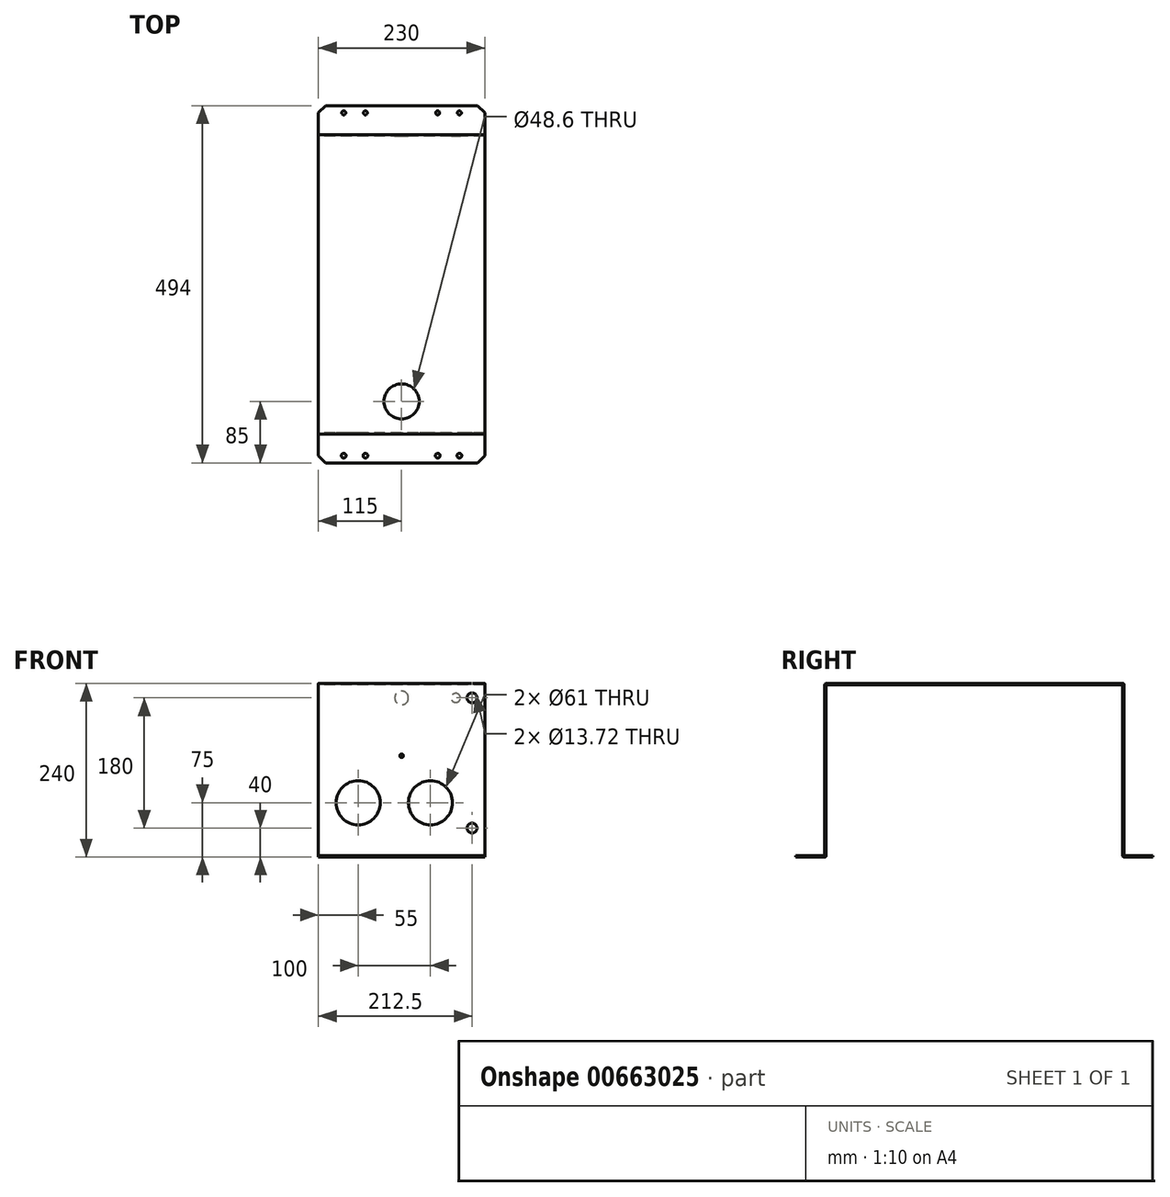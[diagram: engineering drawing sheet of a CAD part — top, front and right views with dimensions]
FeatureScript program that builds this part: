
annotation { "Feature Type Name" : "Feature", "Feature Type Description" : "" }
export const myFeature = defineFeature(function(context is Context, id is Id, definition is map)
    precondition{}
    {
        {
            var Q0;
            Q0=qCreatedBy(makeId("Right.planeOp"),FACE);
            var sketch = newSketch(context, id + "F0", { "sketchPlane" : qUnion([Q0])});
            skLineSegment(sketch, "E0", {"start": v(-205, 0) * mm, "end": v(205, 0) * mm});
            skLineSegment(sketch, "E1", {"start": v(207, -2) * mm, "end": v(207, -238) * mm});
            skLineSegment(sketch, "E2", {"start": v(-207, -2) * mm, "end": v(-207, -238) * mm});
            skLineSegment(sketch, "E3", {"start": v(-207, -238) * mm, "end": v(-247, -238) * mm});
            skLineSegment(sketch, "E4", {"start": v(207, -238) * mm, "end": v(247, -238) * mm});
            skLineSegment(sketch, "E5.0", {"start": v(207, -240) * mm, "end": v(247, -240) * mm});
            skLineSegment(sketch, "E5.1", {"start": v(-207, -240) * mm, "end": v(-247, -240) * mm});
            skLineSegment(sketch, "E5.2", {"start": v(-205, -2) * mm, "end": v(-205, -238) * mm});
            skLineSegment(sketch, "E5.3", {"start": v(-205, -2) * mm, "end": v(205, -2) * mm});
            skLineSegment(sketch, "E5.4", {"start": v(205, -2) * mm, "end": v(205, -238) * mm});
            skLineSegment(sketch, "E6", {"start": v(247, -238) * mm, "end": v(247, -240) * mm});
            skLineSegment(sketch, "E7", {"start": v(-247, -238) * mm, "end": v(-247, -240) * mm});
            skPoint(sketch, "E8.visualSharp", {"position": v(-207, 0) * mm});
            skArc(sketch, "E8.filletArc", {"start": v(-205, 0) * mm, "mid": v(-206.41, -0.59) * mm, "end": v(-207, -2) * mm});
            skPoint(sketch, "E9.visualSharp", {"position": v(207, 0) * mm});
            skArc(sketch, "E9.filletArc", {"start": v(207, -2) * mm, "mid": v(206.41, -0.59) * mm, "end": v(205, 0) * mm});
            skPoint(sketch, "E10.visualSharp", {"position": v(205, -240) * mm});
            skArc(sketch, "E10.filletArc", {"start": v(205, -238) * mm, "mid": v(205.59, -239.41) * mm, "end": v(207, -240) * mm});
            skPoint(sketch, "E11.visualSharp", {"position": v(-205, -240) * mm});
            skArc(sketch, "E11.filletArc", {"start": v(-207, -240) * mm, "mid": v(-205.59, -239.41) * mm, "end": v(-205, -238) * mm});
            skSolve(sketch);
        }
        {
            var Q0;
            Q0=makeQuery(id+"F0.imprint","IMPRINT",FACE,{"disambiguationData":[TD([[makeQuery(id+"F0.imprint","IMPRINT",EDGE,{"derivedFrom":sQuery(id+"F0.wireOp",EDGE,"E0")}),-1.0]])]});
            extrude(context, id + "F1", {"entities" : qUnion([Q0]), "depth" : 230 * mm, "offsetDistance" : 25 * mm});
        }
        {
            var Q0;
            Q0=makeQuery(id+"F1.opExtrude","SWEPT_FACE",FACE,{"disambiguationData":[OSD([sQuery(id+"F0.wireOp",EDGE,"E0")])]});
            var sketch = newSketch(context, id + "F2", { "sketchPlane" : qUnion([Q0])});
            skPoint(sketch, "E12", {"position": v(115, -162) * mm});
            skSolve(sketch);
        }
        {
            var Q0;
            Q0=sQuery(id+"F2.wireOp",VERTEX,"E12");
            var Q1;
            Q1=makeQuery(id+"F1.opExtrude","SWEPT_BODY",BODY,{"disambiguationData":[OSD([sQuery(id+"F0.wireOp",EDGE,"E0"),sQuery(id+"F0.wireOp",EDGE,"E1"),sQuery(id+"F0.wireOp",EDGE,"E2"),sQuery(id+"F0.wireOp",EDGE,"E3"),sQuery(id+"F0.wireOp",EDGE,"E4"),sQuery(id+"F0.wireOp",EDGE,"E5.0"),sQuery(id+"F0.wireOp",EDGE,"E5.1"),sQuery(id+"F0.wireOp",EDGE,"E5.2"),sQuery(id+"F0.wireOp",EDGE,"E5.3"),sQuery(id+"F0.wireOp",EDGE,"E5.4"),sQuery(id+"F0.wireOp",EDGE,"E6"),sQuery(id+"F0.wireOp",EDGE,"E7"),sQuery(id+"F0.wireOp",EDGE,"E8.filletArc"),sQuery(id+"F0.wireOp",EDGE,"E9.filletArc"),sQuery(id+"F0.wireOp",EDGE,"E10.filletArc"),sQuery(id+"F0.wireOp",EDGE,"E11.filletArc")])]});
            hole(context, id + "F3", {"style" : HoleStyle.SIMPLE, "endStyle" : HoleEndStyle.THROUGH, "holeDiameter" : 48.6 * mm, "majorDiameter" : 5 * mm, "isTappedThrough" : true, "tappedDepth" : 12 * mm, "tapClearance" : 3, "locations" : qUnion([Q0]), "scope" : qUnion([Q1])});
        }
        {
            var Q0;
            Q0=makeQuery(id+"F1.opExtrude","SWEPT_FACE",FACE,{"disambiguationData":[OSD([sQuery(id+"F0.wireOp",EDGE,"E3")])]});
            var sketch = newSketch(context, id + "F4", { "sketchPlane" : qUnion([Q0])});
            skPoint(sketch, "E13", {"position": v(35, -237) * mm});
            skPoint(sketch, "E14", {"position": v(65, -237) * mm});
            skPoint(sketch, "E15", {"position": v(165, -237) * mm});
            skPoint(sketch, "E16", {"position": v(195, -237) * mm});
            skPoint(sketch, "E17", {"position": v(35, 237) * mm});
            skPoint(sketch, "E18", {"position": v(65, 237) * mm});
            skPoint(sketch, "E19", {"position": v(165, 237) * mm});
            skPoint(sketch, "E20", {"position": v(195, 237) * mm});
            skSolve(sketch);
        }
        {
            var Q0;
            Q0=sQuery(id+"F4.wireOp",VERTEX,"E13");
            var Q1;
            Q1=sQuery(id+"F4.wireOp",VERTEX,"E14");
            var Q2;
            Q2=sQuery(id+"F4.wireOp",VERTEX,"E15");
            var Q3;
            Q3=sQuery(id+"F4.wireOp",VERTEX,"E16");
            var Q4;
            Q4=makeQuery(id+"F1.opExtrude","SWEPT_BODY",BODY,{"disambiguationData":[OSD([sQuery(id+"F0.wireOp",EDGE,"E0"),sQuery(id+"F0.wireOp",EDGE,"E1"),sQuery(id+"F0.wireOp",EDGE,"E2"),sQuery(id+"F0.wireOp",EDGE,"E3"),sQuery(id+"F0.wireOp",EDGE,"E4"),sQuery(id+"F0.wireOp",EDGE,"E5.0"),sQuery(id+"F0.wireOp",EDGE,"E5.1"),sQuery(id+"F0.wireOp",EDGE,"E5.2"),sQuery(id+"F0.wireOp",EDGE,"E5.3"),sQuery(id+"F0.wireOp",EDGE,"E5.4"),sQuery(id+"F0.wireOp",EDGE,"E6"),sQuery(id+"F0.wireOp",EDGE,"E7"),sQuery(id+"F0.wireOp",EDGE,"E8.filletArc"),sQuery(id+"F0.wireOp",EDGE,"E9.filletArc"),sQuery(id+"F0.wireOp",EDGE,"E10.filletArc"),sQuery(id+"F0.wireOp",EDGE,"E11.filletArc")])]});
            hole(context, id + "F5", {"style" : HoleStyle.SIMPLE, "endStyle" : HoleEndStyle.THROUGH, "holeDiameter" : 6.5 * mm, "majorDiameter" : 5 * mm, "isTappedThrough" : true, "tappedDepth" : 12 * mm, "tapClearance" : 3, "locations" : qUnion([Q0, Q1, Q2, Q3]), "scope" : qUnion([Q4])});
        }
        {
            var Q0;
            Q0=sQuery(id+"F4.wireOp",VERTEX,"E17");
            var Q1;
            Q1=sQuery(id+"F4.wireOp",VERTEX,"E18");
            var Q2;
            Q2=sQuery(id+"F4.wireOp",VERTEX,"E19");
            var Q3;
            Q3=sQuery(id+"F4.wireOp",VERTEX,"E20");
            var Q4;
            Q4=makeQuery(id+"F1.opExtrude","SWEPT_BODY",BODY,{"disambiguationData":[OSD([sQuery(id+"F0.wireOp",EDGE,"E0"),sQuery(id+"F0.wireOp",EDGE,"E1"),sQuery(id+"F0.wireOp",EDGE,"E2"),sQuery(id+"F0.wireOp",EDGE,"E3"),sQuery(id+"F0.wireOp",EDGE,"E4"),sQuery(id+"F0.wireOp",EDGE,"E5.0"),sQuery(id+"F0.wireOp",EDGE,"E5.1"),sQuery(id+"F0.wireOp",EDGE,"E5.2"),sQuery(id+"F0.wireOp",EDGE,"E5.3"),sQuery(id+"F0.wireOp",EDGE,"E5.4"),sQuery(id+"F0.wireOp",EDGE,"E6"),sQuery(id+"F0.wireOp",EDGE,"E7"),sQuery(id+"F0.wireOp",EDGE,"E8.filletArc"),sQuery(id+"F0.wireOp",EDGE,"E9.filletArc"),sQuery(id+"F0.wireOp",EDGE,"E10.filletArc"),sQuery(id+"F0.wireOp",EDGE,"E11.filletArc")])]});
            hole(context, id + "F6", {"style" : HoleStyle.SIMPLE, "endStyle" : HoleEndStyle.THROUGH, "holeDiameter" : 5.5 * mm, "majorDiameter" : 5 * mm, "isTappedThrough" : true, "tappedDepth" : 12 * mm, "tapClearance" : 3, "locations" : qUnion([Q0, Q1, Q2, Q3]), "scope" : qUnion([Q4])});
        }
        {
            var Q0;
            Q0=makeQuery(id+"F1.opExtrude","CAP_EDGE",EDGE,{"disambiguationData":[OSD([sQuery(id+"F0.wireOp",EDGE,"E7")])],"isStart":true});
            var Q1;
            Q1=makeQuery(id+"F1.opExtrude","CAP_EDGE",EDGE,{"disambiguationData":[OSD([sQuery(id+"F0.wireOp",EDGE,"E7")])],"isStart":false});
            var Q2;
            Q2=makeQuery(id+"F1.opExtrude","CAP_EDGE",EDGE,{"disambiguationData":[OSD([sQuery(id+"F0.wireOp",EDGE,"E6")])],"isStart":false});
            var Q3;
            Q3=makeQuery(id+"F1.opExtrude","CAP_EDGE",EDGE,{"disambiguationData":[OSD([sQuery(id+"F0.wireOp",EDGE,"E6")])],"isStart":true});
            chamfer(context, id + "F7", {"entities" : qUnion([Q0, Q1, Q2, Q3]), "width" : 10 * mm, "tangentPropagation" : true});
        }
        {
            var Q0;
            Q0=makeQuery(id+"F1.opExtrude","SWEPT_FACE",FACE,{"disambiguationData":[OSD([sQuery(id+"F0.wireOp",EDGE,"E2")])]});
            var sketch = newSketch(context, id + "F8", { "sketchPlane" : qUnion([Q0])});
            skPoint(sketch, "E21", {"position": v(55, -165) * mm});
            skPoint(sketch, "E22", {"position": v(155, -165) * mm});
            skPoint(sketch, "E23", {"position": v(212.5, -20) * mm});
            skPoint(sketch, "E24", {"position": v(212.5, -200) * mm});
            skPoint(sketch, "E25", {"position": v(115, -100) * mm});
            skSolve(sketch);
        }
        {
            var Q0;
            Q0=sQuery(id+"F8.wireOp",VERTEX,"E21");
            var Q1;
            Q1=sQuery(id+"F8.wireOp",VERTEX,"E22");
            var Q2;
            Q2=makeQuery(id+"F1.opExtrude","SWEPT_BODY",BODY,{"disambiguationData":[OSD([sQuery(id+"F0.wireOp",EDGE,"E0"),sQuery(id+"F0.wireOp",EDGE,"E1"),sQuery(id+"F0.wireOp",EDGE,"E2"),sQuery(id+"F0.wireOp",EDGE,"E3"),sQuery(id+"F0.wireOp",EDGE,"E4"),sQuery(id+"F0.wireOp",EDGE,"E5.0"),sQuery(id+"F0.wireOp",EDGE,"E5.1"),sQuery(id+"F0.wireOp",EDGE,"E5.2"),sQuery(id+"F0.wireOp",EDGE,"E5.3"),sQuery(id+"F0.wireOp",EDGE,"E5.4"),sQuery(id+"F0.wireOp",EDGE,"E6"),sQuery(id+"F0.wireOp",EDGE,"E7"),sQuery(id+"F0.wireOp",EDGE,"E8.filletArc"),sQuery(id+"F0.wireOp",EDGE,"E9.filletArc"),sQuery(id+"F0.wireOp",EDGE,"E10.filletArc"),sQuery(id+"F0.wireOp",EDGE,"E11.filletArc")])]});
            hole(context, id + "F9", {"style" : HoleStyle.SIMPLE, "endStyle" : HoleEndStyle.BLIND, "holeDiameter" : 61 * mm, "majorDiameter" : 5 * mm, "holeDepth" : 12 * mm, "isTappedThrough" : true, "tappedDepth" : 12 * mm, "tapClearance" : 3, "locations" : qUnion([Q0, Q1]), "scope" : qUnion([Q2])});
        }
        {
            var Q0;
            Q0=sQuery(id+"F8.wireOp",VERTEX,"E25");
            var Q1;
            Q1=makeQuery(id+"F1.opExtrude","SWEPT_BODY",BODY,{"disambiguationData":[OSD([sQuery(id+"F0.wireOp",EDGE,"E0"),sQuery(id+"F0.wireOp",EDGE,"E1"),sQuery(id+"F0.wireOp",EDGE,"E2"),sQuery(id+"F0.wireOp",EDGE,"E3"),sQuery(id+"F0.wireOp",EDGE,"E4"),sQuery(id+"F0.wireOp",EDGE,"E5.0"),sQuery(id+"F0.wireOp",EDGE,"E5.1"),sQuery(id+"F0.wireOp",EDGE,"E5.2"),sQuery(id+"F0.wireOp",EDGE,"E5.3"),sQuery(id+"F0.wireOp",EDGE,"E5.4"),sQuery(id+"F0.wireOp",EDGE,"E6"),sQuery(id+"F0.wireOp",EDGE,"E7"),sQuery(id+"F0.wireOp",EDGE,"E8.filletArc"),sQuery(id+"F0.wireOp",EDGE,"E9.filletArc"),sQuery(id+"F0.wireOp",EDGE,"E10.filletArc"),sQuery(id+"F0.wireOp",EDGE,"E11.filletArc")])]});
            hole(context, id + "F10", {"style" : HoleStyle.SIMPLE, "endStyle" : HoleEndStyle.BLIND, "holeDiameter" : 5 * mm, "majorDiameter" : 5 * mm, "holeDepth" : 5 * mm, "isTappedThrough" : true, "tappedDepth" : 12 * mm, "tapClearance" : 3, "locations" : qUnion([Q0]), "scope" : qUnion([Q1])});
        }
        {
            var Q0;
            Q0=sQuery(id+"F8.wireOp",VERTEX,"E23");
            var Q1;
            Q1=sQuery(id+"F8.wireOp",VERTEX,"E24");
            var Q2;
            Q2=makeQuery(id+"F1.opExtrude","SWEPT_BODY",BODY,{"disambiguationData":[OSD([sQuery(id+"F0.wireOp",EDGE,"E0"),sQuery(id+"F0.wireOp",EDGE,"E1"),sQuery(id+"F0.wireOp",EDGE,"E2"),sQuery(id+"F0.wireOp",EDGE,"E3"),sQuery(id+"F0.wireOp",EDGE,"E4"),sQuery(id+"F0.wireOp",EDGE,"E5.0"),sQuery(id+"F0.wireOp",EDGE,"E5.1"),sQuery(id+"F0.wireOp",EDGE,"E5.2"),sQuery(id+"F0.wireOp",EDGE,"E5.3"),sQuery(id+"F0.wireOp",EDGE,"E5.4"),sQuery(id+"F0.wireOp",EDGE,"E6"),sQuery(id+"F0.wireOp",EDGE,"E7"),sQuery(id+"F0.wireOp",EDGE,"E8.filletArc"),sQuery(id+"F0.wireOp",EDGE,"E9.filletArc"),sQuery(id+"F0.wireOp",EDGE,"E10.filletArc"),sQuery(id+"F0.wireOp",EDGE,"E11.filletArc")])]});
            hole(context, id + "F11", {"style" : HoleStyle.SIMPLE, "endStyle" : HoleEndStyle.BLIND, "holeDiameter" : 13.72 * mm, "majorDiameter" : 5 * mm, "holeDepth" : 5 * mm, "isTappedThrough" : true, "tappedDepth" : 12 * mm, "tapClearance" : 3, "locations" : qUnion([Q0, Q1]), "scope" : qUnion([Q2])});
        }
        {
            var Q0;
            Q0=makeQuery(id+"F1.opExtrude","SWEPT_FACE",FACE,{"disambiguationData":[OSD([sQuery(id+"F0.wireOp",EDGE,"E1")])]});
            var sketch = newSketch(context, id + "F12", { "sketchPlane" : qUnion([Q0])});
            skPoint(sketch, "E26", {"position": v(-190, -20) * mm});
            skPoint(sketch, "E27", {"position": v(-115, -20) * mm});
            skSolve(sketch);
        }
        {
            var Q0;
            Q0=sQuery(id+"F12.wireOp",VERTEX,"E26");
            var Q1;
            Q1=makeQuery(id+"F1.opExtrude","SWEPT_BODY",BODY,{"disambiguationData":[OSD([sQuery(id+"F0.wireOp",EDGE,"E0"),sQuery(id+"F0.wireOp",EDGE,"E1"),sQuery(id+"F0.wireOp",EDGE,"E2"),sQuery(id+"F0.wireOp",EDGE,"E3"),sQuery(id+"F0.wireOp",EDGE,"E4"),sQuery(id+"F0.wireOp",EDGE,"E5.0"),sQuery(id+"F0.wireOp",EDGE,"E5.1"),sQuery(id+"F0.wireOp",EDGE,"E5.2"),sQuery(id+"F0.wireOp",EDGE,"E5.3"),sQuery(id+"F0.wireOp",EDGE,"E5.4"),sQuery(id+"F0.wireOp",EDGE,"E6"),sQuery(id+"F0.wireOp",EDGE,"E7"),sQuery(id+"F0.wireOp",EDGE,"E8.filletArc"),sQuery(id+"F0.wireOp",EDGE,"E9.filletArc"),sQuery(id+"F0.wireOp",EDGE,"E10.filletArc"),sQuery(id+"F0.wireOp",EDGE,"E11.filletArc")])]});
            hole(context, id + "F13", {"style" : HoleStyle.SIMPLE, "endStyle" : HoleEndStyle.BLIND, "holeDiameter" : 12.7 * mm, "majorDiameter" : 5 * mm, "holeDepth" : 5 * mm, "isTappedThrough" : true, "tappedDepth" : 12 * mm, "tapClearance" : 3, "locations" : qUnion([Q0]), "scope" : qUnion([Q1])});
        }
        {
            var Q0;
            Q0=sQuery(id+"F12.wireOp",VERTEX,"E27");
            var Q1;
            Q1=makeQuery(id+"F1.opExtrude","SWEPT_BODY",BODY,{"disambiguationData":[OSD([sQuery(id+"F0.wireOp",EDGE,"E0"),sQuery(id+"F0.wireOp",EDGE,"E1"),sQuery(id+"F0.wireOp",EDGE,"E2"),sQuery(id+"F0.wireOp",EDGE,"E3"),sQuery(id+"F0.wireOp",EDGE,"E4"),sQuery(id+"F0.wireOp",EDGE,"E5.0"),sQuery(id+"F0.wireOp",EDGE,"E5.1"),sQuery(id+"F0.wireOp",EDGE,"E5.2"),sQuery(id+"F0.wireOp",EDGE,"E5.3"),sQuery(id+"F0.wireOp",EDGE,"E5.4"),sQuery(id+"F0.wireOp",EDGE,"E6"),sQuery(id+"F0.wireOp",EDGE,"E7"),sQuery(id+"F0.wireOp",EDGE,"E8.filletArc"),sQuery(id+"F0.wireOp",EDGE,"E9.filletArc"),sQuery(id+"F0.wireOp",EDGE,"E10.filletArc"),sQuery(id+"F0.wireOp",EDGE,"E11.filletArc")])]});
            hole(context, id + "F14", {"style" : HoleStyle.SIMPLE, "endStyle" : HoleEndStyle.BLIND, "holeDiameter" : 19.05 * mm, "majorDiameter" : 5 * mm, "holeDepth" : 5 * mm, "isTappedThrough" : true, "tappedDepth" : 12 * mm, "tapClearance" : 3, "locations" : qUnion([Q0]), "scope" : qUnion([Q1])});
        }
    });
